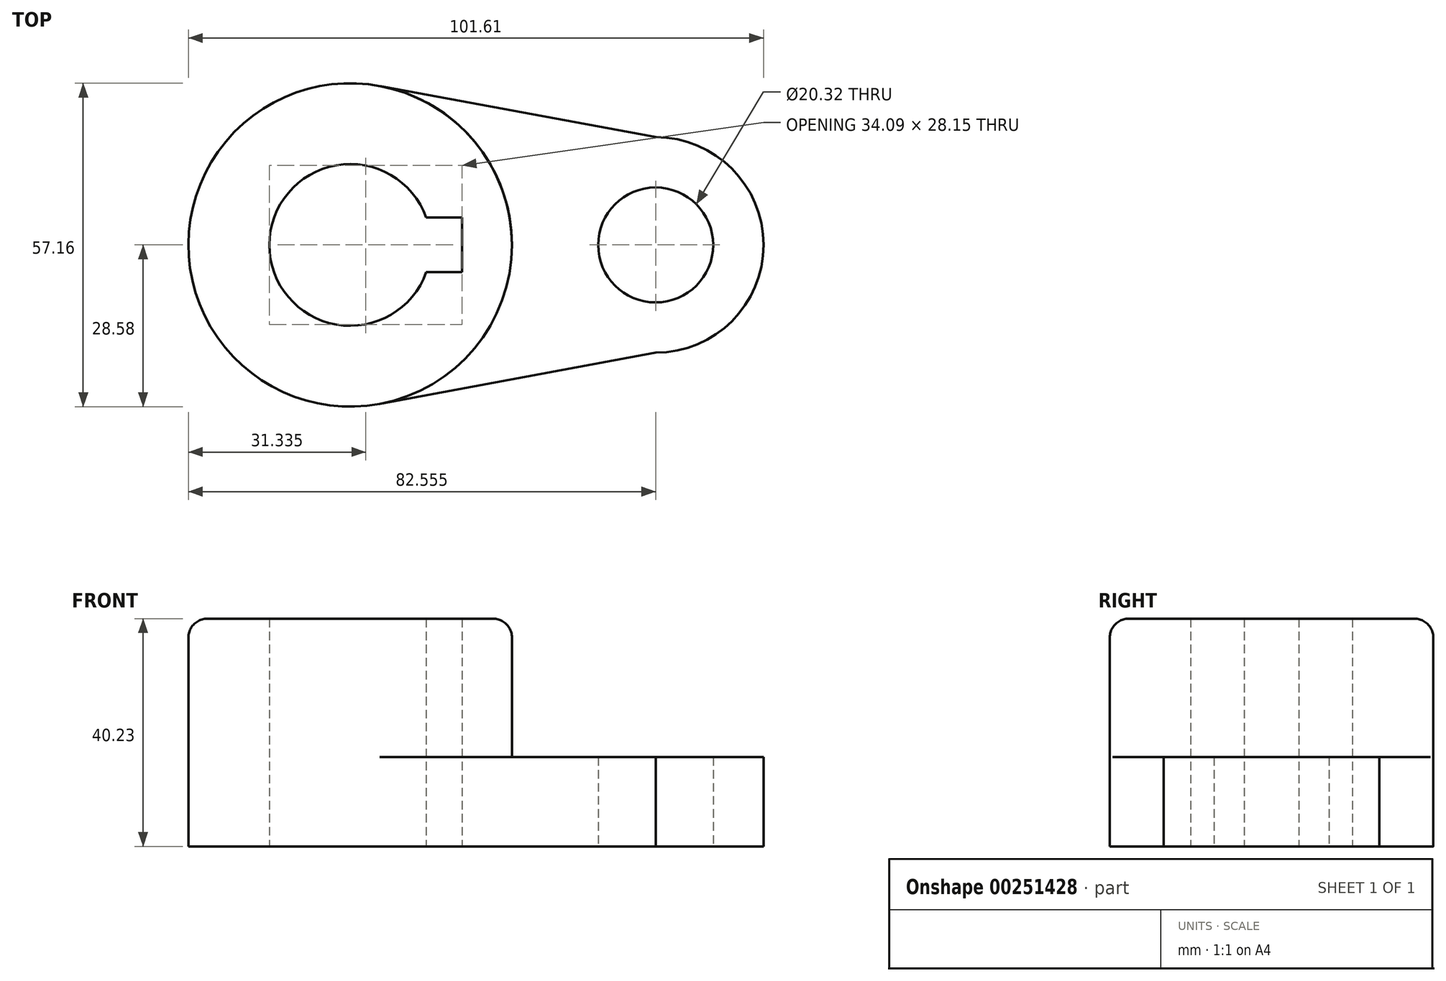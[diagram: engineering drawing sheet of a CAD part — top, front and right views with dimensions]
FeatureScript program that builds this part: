
annotation { "Feature Type Name" : "Feature", "Feature Type Description" : "" }
export const myFeature = defineFeature(function(context is Context, id is Id, definition is map)
    precondition{}
    {
        {
            var Q0;
            Q0=qCreatedBy(makeId("Top.planeOp"),FACE);
            var sketch = newSketch(context, id + "F0", { "sketchPlane" : qUnion([Q0])});
            skArc(sketch, "E0", {"start": v(13.45, 4.83) * mm, "mid": v(-14.29, 0) * mm, "end": v(13.45, -4.83) * mm});
            skCircle(sketch, "E1", {"center": v(53.98, 0) * mm, "radius": 10.16 * mm});
            skCircle(sketch, "E2", {"center": v(0, 0) * mm, "radius": 28.58 * mm});
            skCircle(sketch, "E3", {"center": v(53.98, 0) * mm, "radius": 19.05 * mm});
            skPoint(sketch, "E4.visualSharp", {"position": v(33.04, -28.58) * mm});
            skLineSegment(sketch, "E5.right", {"start": v(19.8, -4.83) * mm, "end": v(19.8, 4.83) * mm});
            skLineSegment(sketch, "E6.trimOffspring", {"start": v(13.45, 4.83) * mm, "end": v(19.8, 4.83) * mm});
            skLineSegment(sketch, "E7.trimOffspring", {"start": v(13.45, -4.83) * mm, "end": v(19.8, -4.83) * mm});
            skLineSegment(sketch, "E8", {"start": v(0, 0) * mm, "end": v(53.97, 0) * mm});
            skLineSegment(sketch, "E9", {"start": v(0, 0) * mm, "end": v(53.98, 0) * mm, "construction": true});
            skLineSegment(sketch, "E10", {"start": v(53.97, -19.05) * mm, "end": v(5.21, -28.1) * mm});
            skLineSegment(sketch, "E11", {"start": v(53.98, 19.05) * mm, "end": v(5.21, 28.1) * mm});
            skSolve(sketch);
        }
        {
            var Q0;
            Q0=makeQuery(id+"F0.imprint","IMPRINT",FACE,{"disambiguationData":[TD([[makeQuery(id+"F0.imprint","IMPRINT",EDGE,{"derivedFrom":sQuery(id+"F0.wireOp",EDGE,"E0")}),-1.0]])]});
            extrude(context, id + "F1", {"entities" : qUnion([Q0]), "depth" : 40.23 * mm});
        }
        {
            var Q0;
            {var subQ0=sQuery(id+"F0.wireOp",EDGE,"o5OdITKO-bEnJ-2VYi-a7Jk-zIUuU5JH3HSI");var subQ1=sQuery(id+"F0.wireOp",EDGE,"E2");var subQ2=makeQuery(id+"F0.imprint","INTERSECT",VERTEX,{"disambiguationData":[OD(1.0)],"derivedFrom":[subQ1,subQ0]});Q0=makeQuery(id+"F0.imprint","IMPRINT",FACE,{"disambiguationData":[TD([[makeQuery(id+"F0.imprint","IMPRINT",EDGE,{"disambiguationData":[TD([[subQ2,1.0]])],"derivedFrom":subQ1}),-1.0]])]});}
            var Q1;
            Q1=makeQuery(id+"F0.imprint","IMPRINT",FACE,{"disambiguationData":[TD([[makeQuery(id+"F0.imprint","IMPRINT",EDGE,{"derivedFrom":sQuery(id+"F0.wireOp",EDGE,"E1")}),-1.0]])]});
            extrude(context, id + "F2", {"entities" : qUnion([Q0, Q1]), "operationType" : NewBodyOperationType.ADD, "depth" : 15.77 * mm});
        }
        {
            var Q0;
            {var subQ0=sQuery(id+"F0.wireOp",EDGE,"E2");Q0=makeQuery(id+"F1.opExtrude","CAP_EDGE",EDGE,{"disambiguationData":[OSD([subQ0]),TDD([makeQuery(id+"F0.imprint","IMPRINT",EDGE,{"disambiguationData":[TD([[makeQuery(id+"F0.imprint","INTERSECT",VERTEX,{"disambiguationData":[OD(0.0)],"derivedFrom":[subQ0,sQuery(id+"F0.wireOp",EDGE,"SRnHb5uK-vhAm-8B8o-SrwD-EHZrL22LgCVp")]}),1.0]])],"derivedFrom":subQ0})])],"isStart":false});}
            var Q1;
            Q1=makeQuery(id+"F1.opExtrude","CAP_EDGE",EDGE,{"disambiguationData":[OSD([sQuery(id+"F0.wireOp",EDGE,"SRnHb5uK-vhAm-8B8o-SrwD-EHZrL22LgCVp")])],"isStart":false});
            var Q2;
            {var subQ0=sQuery(id+"F0.wireOp",EDGE,"E2");Q2=makeQuery(id+"F1.opExtrude","CAP_EDGE",EDGE,{"disambiguationData":[OSD([subQ0]),TDD([makeQuery(id+"F0.imprint","IMPRINT",EDGE,{"disambiguationData":[TD([[makeQuery(id+"F0.imprint","INTERSECT",VERTEX,{"disambiguationData":[OD(1.0)],"derivedFrom":[subQ0,sQuery(id+"F0.wireOp",EDGE,"o5OdITKO-bEnJ-2VYi-a7Jk-zIUuU5JH3HSI")]}),1.0]])],"derivedFrom":subQ0})])],"isStart":false});}
            var Q3;
            Q3=makeQuery(id+"F1.opExtrude","CAP_EDGE",EDGE,{"disambiguationData":[OSD([sQuery(id+"F0.wireOp",EDGE,"o5OdITKO-bEnJ-2VYi-a7Jk-zIUuU5JH3HSI")])],"isStart":false});
            fillet(context, id + "F3", {"entities" : qUnion([Q0, Q1, Q2, Q3]), "radius" : 3.3 * mm, "tangentPropagation" : true, "allowEdgeOverflow" : false});
        }
    });
